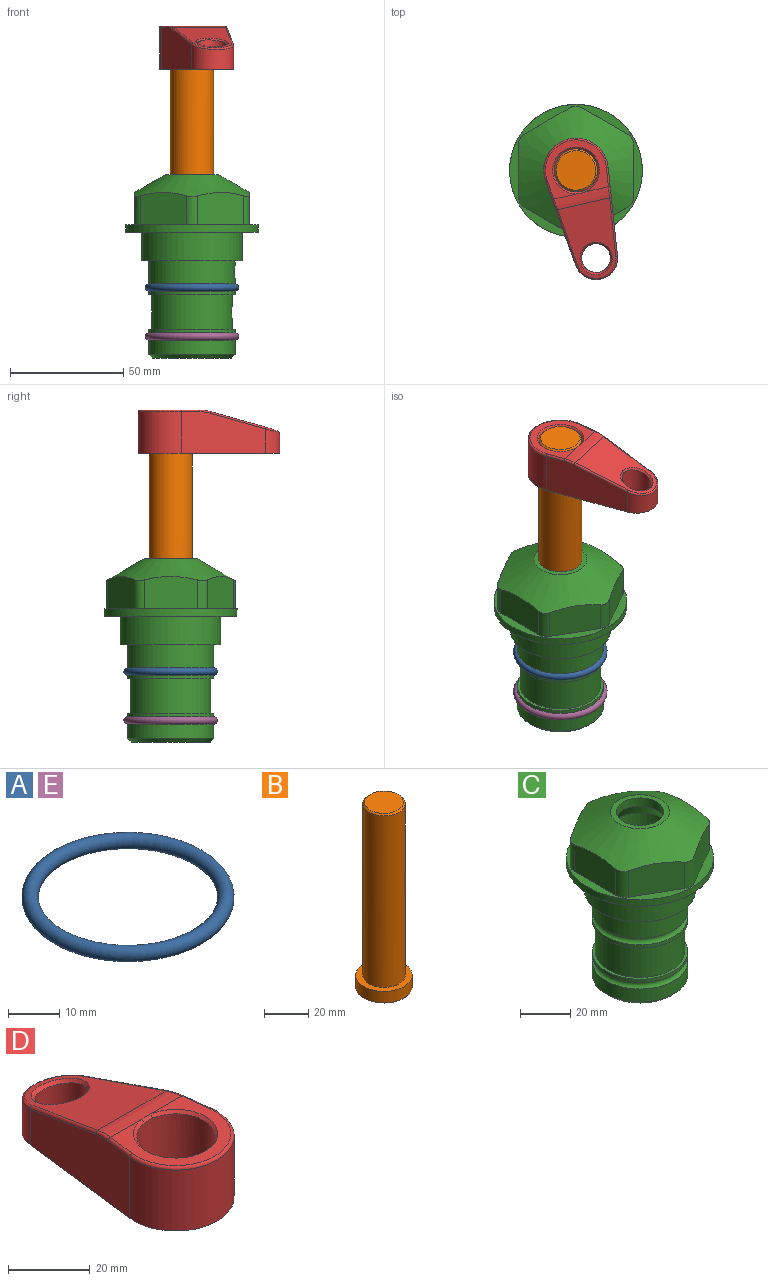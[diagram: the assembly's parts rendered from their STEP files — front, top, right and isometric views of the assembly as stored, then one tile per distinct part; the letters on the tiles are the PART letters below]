
ASSEMBLY  parts=5 mates=4
PART A: 1 faces, bbox 44.7x44.7x3.2 mm
  f0: torus R=19.05mm, axis (0,0,1), area 1193.9mm2
PART B: 6 faces, bbox 25.4x25.4x101.6 mm
  f0: plane 17.46x17.46mm, normal (0,0,1), area 239.5mm2, adj f5
  f1: plane 25.4x25.4mm, normal (0,0,-1), area 506.7mm2, adj f2
  f2: cylinder r=12.7mm len=25.4mm, axis (0,0,1), area 506.7mm2, adj f1,f3
  f3: plane 25.4x25.4mm, normal (0,0,1), area 221.7mm2, adj f2,f4
  f4: cylinder r=9.53mm len=94.46mm, axis (0,0,1), area 5653mm2, adj f3,f5
  f5: cone r=8.73mm half-angle=45deg, axis (0,0,-1), area 64.4mm2, adj f0,f4
PART C: 36 faces, bbox 58.7x58.7x81 mm
  f0: cylinder r=17.78mm len=35.56mm, axis (0,0,1), area 1670.8mm2, adj f23,f24,f31
  f1: cylinder r=19.05mm len=38.1mm, axis (0,0,1), area 1191.9mm2, adj f26,f27,f30
  f2: plane 58.66x58.66mm, normal (0,0,-1), area 1150.6mm2, adj f3,f28
  f3: cylinder r=29.33mm len=58.66mm, axis (0,0,-1), area 585.1mm2, adj f2,f4
  f4: plane 58.66x58.66mm, normal (0,0,1), area 475.9mm2, adj f3,f5,f6,f7,f8,f9,f10,f11
  f5: plane 20.32x14.34mm, normal (-0.5,0.87,0), area 324.4mm2, adj f4,f15,f16,f17
  f6: plane 20.32x14.34mm, normal (0.5,0.87,0), area 324.4mm2, adj f4,f14,f15,f17
  f7: plane 23.48x14.34mm, normal (1,0,0), area 324.4mm2, adj f4,f13,f14,f17
  f8: plane 20.32x14.34mm, normal (0.5,-0.87,0), area 324.4mm2, adj f4,f12,f13,f17
  f9: plane 20.32x14.34mm, normal (-0.5,-0.87,0), area 324.4mm2, adj f4,f11,f12,f17
  f10: plane 23.48x14.34mm, normal (-1,0,0), area 324.4mm2, adj f4,f11,f16,f17
  f11: cylinder r=5.08mm len=12.85mm, axis (0,0,-1), area 67.2mm2, adj f4,f9,f10,f17
  f12: cylinder r=5.08mm len=12.85mm, axis (0,0,-1), area 67.2mm2, adj f4,f8,f9,f17
  f13: cylinder r=5.08mm len=12.85mm, axis (0,0,-1), area 67.2mm2, adj f4,f7,f8,f17
  f14: cylinder r=5.08mm len=12.85mm, axis (0,0,-1), area 67.2mm2, adj f4,f6,f7,f17
  f15: cylinder r=5.08mm len=12.85mm, axis (0,0,-1), area 67.2mm2, adj f4,f5,f6,f17
  f16: cylinder r=5.08mm len=12.85mm, axis (0,0,-1), area 67.2mm2, adj f4,f5,f10,f17
  f17: cone r=11.73mm half-angle=60deg, axis (0,0,-1), area 2071.8mm2, adj f5,f6,f7,f8,f9,f10,f11,f12
  f18: plane 23.46x23.46mm, normal (0,0,1), area 147.4mm2, adj f17,f35
  f19: plane 34.93x34.93mm, normal (0,0,-1), area 958mm2, adj f29
  f20: cylinder r=19.05mm len=38.1mm, axis (0,0,1), area 760.1mm2, adj f21,f29
  f21: torus R=19.05mm, axis (0,0,1), area 565.3mm2, adj f20,f22
  f22: cylinder r=19.05mm len=38.1mm, axis (0,0,1), area 190mm2, adj f21,f23
  f23: plane 38.1x38.1mm, normal (0,0,1), area 146.9mm2, adj f0,f22
  f24: plane 38.1x38.1mm, normal (0,0,-1), area 146.9mm2, adj f0,f25
  f25: cylinder r=19.05mm len=38.1mm, axis (0,0,1), area 190mm2, adj f24,f26
  f26: torus R=19.05mm, axis (0,0,1), area 565.3mm2, adj f1,f25
  f27: plane 44.45x44.45mm, normal (0,0,-1), area 411.7mm2, adj f1,f28
  f28: cylinder r=22.23mm len=44.45mm, axis (0,0,1), area 1773.5mm2, adj f2,f27
  f29: cone r=19.05mm half-angle=45deg, axis (0,0,1), area 257.5mm2, adj f19,f20
  f30: cylinder r=3.17mm len=6.75mm, axis (-1,0,0), area 128mm2, adj f1,f33
  f31: cylinder r=3.17mm len=6.35mm, axis (-1,0,0), area 102.5mm2, adj f0,f33
  f32: plane 25.4x25.4mm, normal (0,0,1), area 506.7mm2, adj f33
  f33: cylinder r=12.7mm len=66.42mm, axis (0,0,-1), area 5236.2mm2, adj f30,f31,f32,f34
  f34: cone r=9.53mm half-angle=30deg, axis (0,0,-1), area 443.4mm2, adj f33,f35
  f35: cylinder r=9.53mm len=19.05mm, axis (0,0,-1), area 240.9mm2, adj f18,f34
PART D: 31 faces, bbox 31.7x65.5x19.8 mm
  f0: plane 39.12x18.26mm, normal (0.99,0.12,0), area 612.2mm2, adj f1,f4,f7,f11,f13,f15
  f1: cylinder r=9.53mm len=18.91mm, axis (0,0,-1), area 296.1mm2, adj f0,f2,f7,f17
  f2: plane 39.12x18.26mm, normal (-0.99,0.12,0), area 612.2mm2, adj f1,f4,f7,f12,f14,f16
  f3: cylinder r=6.35mm len=12.7mm, axis (0,0,-1), area 362.4mm2, adj f7,f18
  f4: cylinder r=14.29mm len=28.58mm, axis (0,0,-1), area 882.2mm2, adj f0,f2,f7,f10
  f5: cylinder r=9.53mm len=19.05mm, axis (0,0,-1), area 1092.6mm2, adj f7,f19,f20
  f6: plane 26.99x23.69mm, normal (0,0,1), area 216.2mm2, adj f9,f10,f11,f12,f19
  f7: plane 63.5x28.58mm, normal (0,0,-1), area 661.8mm2, adj f0,f1,f2,f3,f4,f5,f22,f23
  f8: plane 33.52x23.6mm, normal (0,0.26,0.97), area 486mm2, adj f9,f15,f16,f17,f18
  f9: cylinder r=19.05mm len=24.72mm, axis (1,0,0), area 120.4mm2, adj f6,f8,f13,f14,f20
  f10: torus R=13.49mm, axis (0,0,1), area 59mm2, adj f4,f6,f11,f12
  f11: cylinder r=0.79mm len=8.67mm, axis (0.12,-0.99,0), area 10.8mm2, adj f0,f6,f10,f13
  f12: cylinder r=0.79mm len=8.67mm, axis (0.12,0.99,0), area 10.8mm2, adj f2,f6,f10,f14
  f13: bspline ~4.95x1.42mm, area 6.1mm2, adj f0,f9,f11,f15
  f14: bspline ~4.95x1.42mm, area 6.1mm2, adj f2,f9,f12,f16
  f15: cylinder r=0.79mm len=25.95mm, axis (0.12,-0.96,0.26), area 32.9mm2, adj f0,f8,f13,f17
  f16: cylinder r=0.79mm len=25.95mm, axis (0.12,0.96,-0.26), area 32.9mm2, adj f2,f8,f14,f17
  f17: bspline ~18.91x8.38mm, area 30mm2, adj f1,f8,f15,f16
  f18: bspline ~14.29x14.29mm, area 48.3mm2, adj f3,f8
  f19: cone r=9.53mm half-angle=45deg, axis (0,0,1), area 66.5mm2, adj f5,f6,f20
  f20: bspline ~3.22x0.96mm, area 3.5mm2, adj f5,f9,f19
  f21: plane 2.75x2.72mm, normal (0,0,-1), area 2.9mm2, adj f23,f25,f28
  f22: plane 23.05x15.88mm, normal (-0.99,-0.12,0), area 323.6mm2, adj f7,f25,f26,f27,f28,f29
  f23: plane 23.05x15.88mm, normal (0.99,-0.12,0), area 323.6mm2, adj f7,f21,f25,f27,f28,f30
  f24: cylinder r=9.53mm len=10.69mm, axis (0,0,-1), area 114.7mm2, adj f7,f27,f29,f30
  f25: cylinder r=12.7mm len=20.59mm, axis (0,0,-1), area 381.1mm2, adj f7,f21,f22,f23,f26,f28
  f26: plane 2.75x2.72mm, normal (0,0,-1), area 2.9mm2, adj f22,f25,f28
  f27: plane 19.72x18.37mm, normal (0,-0.26,-0.97), area 291.8mm2, adj f22,f23,f24,f28,f29,f30
  f28: cylinder r=15.88mm len=19.92mm, axis (1,0,0), area 54.8mm2, adj f21,f22,f23,f25,f26,f27
  f29: cylinder r=1.59mm len=11mm, axis (0,0,-1), area 34.7mm2, adj f7,f22,f24,f27
  f30: cylinder r=1.59mm len=11mm, axis (0,0,-1), area 34.7mm2, adj f7,f23,f24,f27
PART E: same geometry as A
PLACE A at identity
PLACE B rot(axis=(0,0,-1),167.1deg) t=(0,0,27.55)mm
PLACE C at identity fixed
PLACE D rot(axis=(0,0,-1),167.1deg) t=(0,0,27.55)mm
PLACE E t=(0,0,-21.59)mm
MATE fastened E.f0 <-> C.f0  axis (0,0,1) through (0,0,-46.1)mm
MATE cylindrical B.f2 <-> C.f0  axis (0,0,-1) through (0,0,-10.55)mm
MATE fastened A.f0 <-> C.f0  axis (0,0,1) through (0,0,-24.51)mm
MATE fastened D.f4 <-> B.f2  axis (0,0,1) through (0,0,91.05)mm
